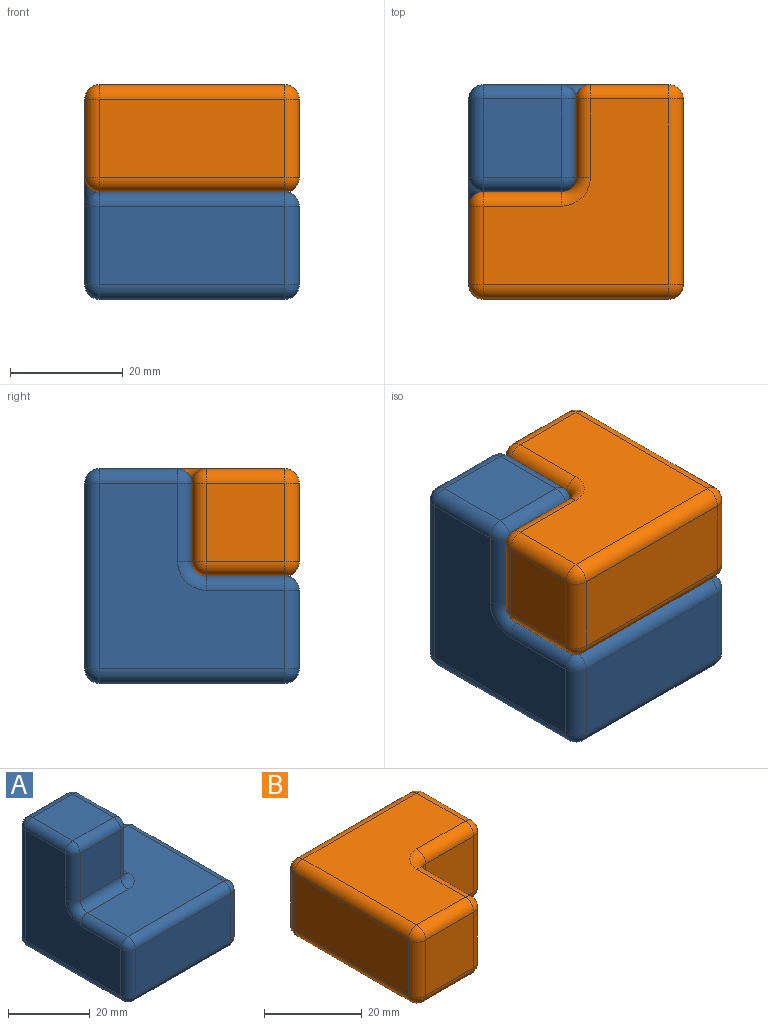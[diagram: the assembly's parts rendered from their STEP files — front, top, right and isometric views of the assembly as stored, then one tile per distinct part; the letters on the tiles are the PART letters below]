
ASSEMBLY  parts=2 mates=1
PART A: 44 faces, bbox 38.1x38.1x38.1 mm
  f0: plane 33.02x33.02mm, normal (0,0,1), area 733mm2, adj f18,f19,f30,f31,f36,f39,f40
  f1: plane 33.02x33.02mm, normal (-1,0,0), area 733mm2, adj f10,f14,f19,f20,f25,f27,f28
  f2: plane 33.02x13.97mm, normal (0,-1,0), area 461.3mm2, adj f9,f10,f17,f18
  f3: plane 33.02x13.97mm, normal (1,0,0), area 461.3mm2, adj f16,f17,f29,f30
  f4: plane 33.02x33.02mm, normal (0,1,0), area 733mm2, adj f15,f28,f29,f38,f39,f42,f43
  f5: plane 33.02x33.02mm, normal (0,0,-1), area 1090.3mm2, adj f9,f14,f15,f16
  f6: plane 13.97x13.97mm, normal (0,-1,0), area 195.2mm2, adj f20,f26,f31,f32
  f7: plane 13.97x13.97mm, normal (1,0,0), area 195.2mm2, adj f32,f37,f40,f43
  f8: plane 13.97x13.97mm, normal (0,0,1), area 195.2mm2, adj f26,f27,f37,f38
  f9: cylinder r=2.54mm len=33.02mm, axis (1,0,0), area 131.7mm2, adj f2,f5,f11,f12
  f10: cylinder r=2.54mm len=13.97mm, axis (0,0,1), area 55.7mm2, adj f1,f2,f11,f13
  f11: sphere r=2.54mm, area 10.1mm2, adj f9,f10,f14
  f12: sphere r=2.54mm, area 10.1mm2, adj f9,f16,f17
  f13: sphere r=2.54mm, area 10.1mm2, adj f10,f18,f19
  f14: cylinder r=2.54mm len=33.02mm, axis (0,-1,0), area 131.7mm2, adj f1,f5,f11,f22
  f15: cylinder r=2.54mm len=33.02mm, axis (-1,0,0), area 131.7mm2, adj f4,f5,f22,f23
  f16: cylinder r=2.54mm len=33.02mm, axis (0,1,0), area 131.7mm2, adj f3,f5,f12,f23
  f17: cylinder r=2.54mm len=13.97mm, axis (0,0,-1), area 55.7mm2, adj f2,f3,f12,f24
  f18: cylinder r=2.54mm len=33.02mm, axis (-1,0,0), area 131.7mm2, adj f0,f2,f13,f24
  f19: cylinder r=2.54mm len=13.97mm, axis (0,1,0), area 55.7mm2, adj f0,f1,f13,f25
  f20: cylinder r=2.54mm len=13.97mm, axis (0,0,1), area 55.7mm2, adj f1,f6,f21,f25
  f21: sphere r=2.54mm, area 10.1mm2, adj f20,f26,f27
  f22: sphere r=2.54mm, area 10.1mm2, adj f14,f15,f28
  f23: sphere r=2.54mm, area 10.1mm2, adj f15,f16,f29
  f24: sphere r=2.54mm, area 10.1mm2, adj f17,f18,f30
  f25: torus R=5.08mm, axis (-1,0,0), area 21.7mm2, adj f1,f19,f20,f31
  f26: cylinder r=2.54mm len=13.97mm, axis (-1,0,0), area 55.7mm2, adj f6,f8,f21,f33
  f27: cylinder r=2.54mm len=13.97mm, axis (0,1,0), area 55.7mm2, adj f1,f8,f21,f34
  f28: cylinder r=2.54mm len=33.02mm, axis (0,0,-1), area 131.7mm2, adj f1,f4,f22,f34
  f29: cylinder r=2.54mm len=13.97mm, axis (0,0,1), area 55.7mm2, adj f3,f4,f23,f35
  f30: cylinder r=2.54mm len=33.02mm, axis (0,-1,0), area 131.7mm2, adj f0,f3,f24,f35
  f31: cylinder r=2.54mm len=13.97mm, axis (1,0,0), area 55.7mm2, adj f0,f6,f25,f36
  f32: cylinder r=2.54mm len=13.97mm, axis (0,0,1), area 55.7mm2, adj f6,f7,f33,f36
  f33: sphere r=2.54mm, area 10.1mm2, adj f26,f32,f37
  f34: sphere r=2.54mm, area 10.1mm2, adj f27,f28,f38
  f35: sphere r=2.54mm, area 10.1mm2, adj f29,f30,f39
  f36: torus R=5.08mm, axis (0,0,1), area 21.7mm2, adj f0,f31,f32,f40
  f37: cylinder r=2.54mm len=13.97mm, axis (0,-1,0), area 55.7mm2, adj f7,f8,f33,f41
  f38: cylinder r=2.54mm len=13.97mm, axis (1,0,0), area 55.7mm2, adj f4,f8,f34,f41
  f39: cylinder r=2.54mm len=13.97mm, axis (1,0,0), area 55.7mm2, adj f0,f4,f35,f42
  f40: cylinder r=2.54mm len=13.97mm, axis (0,1,0), area 55.7mm2, adj f0,f7,f36,f42
  f41: sphere r=2.54mm, area 10.1mm2, adj f37,f38,f43
  f42: torus R=5.08mm, axis (0,1,0), area 21.7mm2, adj f4,f39,f40,f43
  f43: cylinder r=2.54mm len=13.97mm, axis (0,0,-1), area 55.7mm2, adj f4,f7,f41,f42
PART B: 38 faces, bbox 38.1x38.1x19.1 mm
  f0: plane 13.97x13.97mm, normal (0,-1,0), area 195.2mm2, adj f24,f25,f33,f34
  f1: plane 33.02x13.97mm, normal (-1,0,0), area 461.3mm2, adj f11,f12,f21,f22
  f2: plane 33.02x33.02mm, normal (0,0,-1), area 733mm2, adj f8,f11,f15,f20,f25,f26,f30
  f3: plane 13.97x13.97mm, normal (1,0,0), area 195.2mm2, adj f14,f15,f23,f24
  f4: plane 33.02x33.02mm, normal (0,0,1), area 733mm2, adj f13,f22,f23,f32,f33,f36,f37
  f5: plane 33.02x13.97mm, normal (0,1,0), area 461.3mm2, adj f8,f12,f13,f14
  f6: plane 13.97x13.97mm, normal (1,0,0), area 195.2mm2, adj f26,f31,f34,f37
  f7: plane 13.97x13.97mm, normal (0,-1,0), area 195.2mm2, adj f20,f21,f31,f32
  f8: cylinder r=2.54mm len=33.02mm, axis (1,0,0), area 131.7mm2, adj f2,f5,f9,f10
  f9: sphere r=2.54mm, area 10.1mm2, adj f8,f11,f12
  f10: sphere r=2.54mm, area 10.1mm2, adj f8,f14,f15
  f11: cylinder r=2.54mm len=33.02mm, axis (0,-1,0), area 131.7mm2, adj f1,f2,f9,f16
  f12: cylinder r=2.54mm len=13.97mm, axis (0,0,-1), area 55.7mm2, adj f1,f5,f9,f17
  f13: cylinder r=2.54mm len=33.02mm, axis (-1,0,0), area 131.7mm2, adj f4,f5,f17,f18
  f14: cylinder r=2.54mm len=13.97mm, axis (0,0,1), area 55.7mm2, adj f3,f5,f10,f18
  f15: cylinder r=2.54mm len=13.97mm, axis (0,1,0), area 55.7mm2, adj f2,f3,f10,f19
  f16: sphere r=2.54mm, area 10.1mm2, adj f11,f20,f21
  f17: sphere r=2.54mm, area 10.1mm2, adj f12,f13,f22
  f18: sphere r=2.54mm, area 10.1mm2, adj f13,f14,f23
  f19: sphere r=2.54mm, area 10.1mm2, adj f15,f24,f25
  f20: cylinder r=2.54mm len=13.97mm, axis (-1,0,0), area 55.7mm2, adj f2,f7,f16,f27
  f21: cylinder r=2.54mm len=13.97mm, axis (0,0,1), area 55.7mm2, adj f1,f7,f16,f28
  f22: cylinder r=2.54mm len=33.02mm, axis (0,1,0), area 131.7mm2, adj f1,f4,f17,f28
  f23: cylinder r=2.54mm len=13.97mm, axis (0,-1,0), area 55.7mm2, adj f3,f4,f18,f29
  f24: cylinder r=2.54mm len=13.97mm, axis (0,0,-1), area 55.7mm2, adj f0,f3,f19,f29
  f25: cylinder r=2.54mm len=13.97mm, axis (-1,0,0), area 55.7mm2, adj f0,f2,f19,f30
  f26: cylinder r=2.54mm len=13.97mm, axis (0,-1,0), area 55.7mm2, adj f2,f6,f27,f30
  f27: sphere r=2.54mm, area 10.1mm2, adj f20,f26,f31
  f28: sphere r=2.54mm, area 10.1mm2, adj f21,f22,f32
  f29: sphere r=2.54mm, area 10.1mm2, adj f23,f24,f33
  f30: torus R=5.08mm, axis (0,0,1), area 21.7mm2, adj f2,f25,f26,f34
  f31: cylinder r=2.54mm len=13.97mm, axis (0,0,-1), area 55.7mm2, adj f6,f7,f27,f35
  f32: cylinder r=2.54mm len=13.97mm, axis (1,0,0), area 55.7mm2, adj f4,f7,f28,f35
  f33: cylinder r=2.54mm len=13.97mm, axis (1,0,0), area 55.7mm2, adj f0,f4,f29,f36
  f34: cylinder r=2.54mm len=13.97mm, axis (0,0,1), area 55.7mm2, adj f0,f6,f30,f36
  f35: sphere r=2.54mm, area 10.1mm2, adj f31,f32,f37
  f36: torus R=5.08mm, axis (0,0,1), area 21.7mm2, adj f4,f33,f34,f37
  f37: cylinder r=2.54mm len=13.97mm, axis (0,1,0), area 55.7mm2, adj f4,f6,f35,f36
PLACE A t=(18.06,-102.7,2.19)mm
PLACE B rot(axis=(0,0,-1),180deg) t=(56.16,-102.7,21.24)mm
MATE planar A.f6 <-> B.f0  axis (0,-1,0) through (27.58,-83.65,30.76)mm
